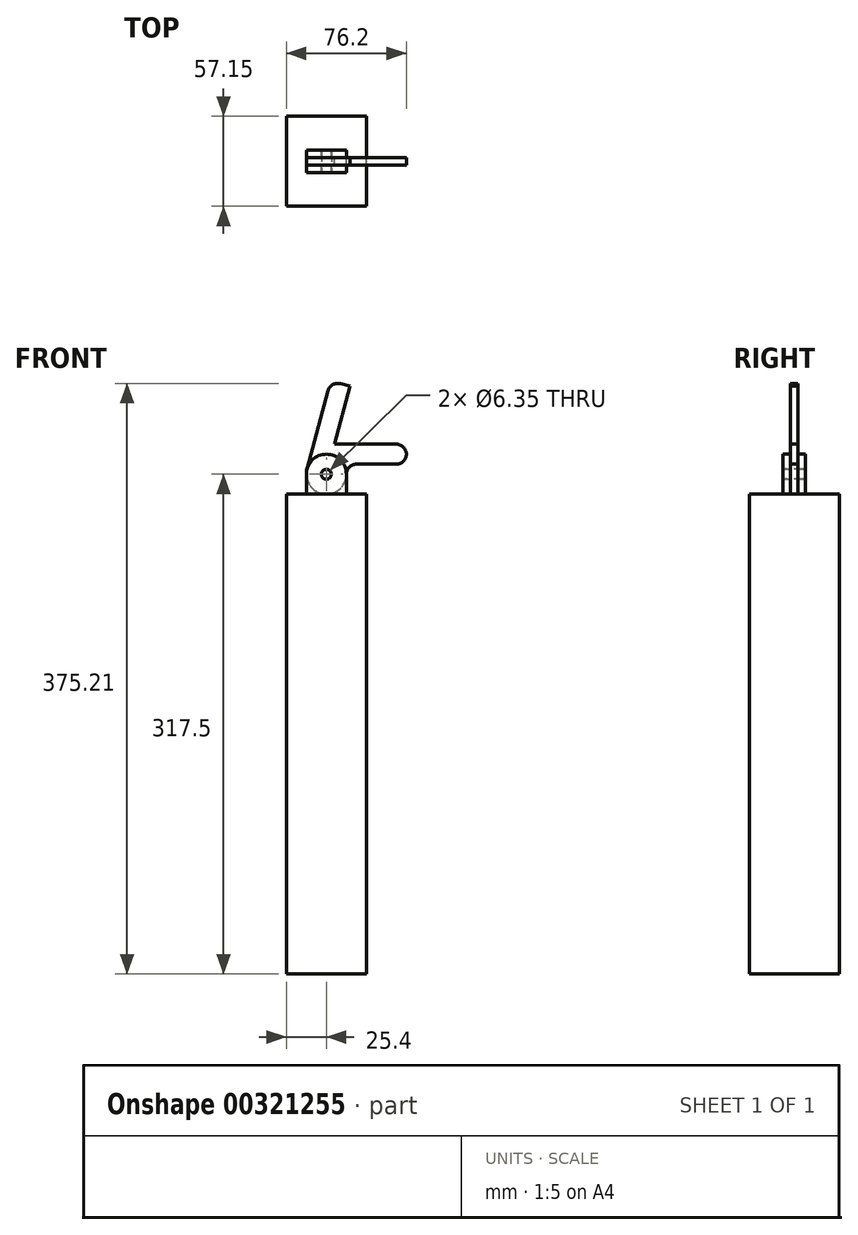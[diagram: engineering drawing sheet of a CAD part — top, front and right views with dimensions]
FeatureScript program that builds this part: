
annotation { "Feature Type Name" : "Feature", "Feature Type Description" : "" }
export const myFeature = defineFeature(function(context is Context, id is Id, definition is map)
    precondition{}
    {
        {
            var Q0;
            Q0=qCreatedBy(makeId("Front.planeOp"),FACE);
            var sketch = newSketch(context, id + "F0", { "sketchPlane" : qUnion([Q0])});
            skCircle(sketch, "E0", {"center": v(0, 0) * mm, "radius": 3.18 * mm});
            skArc(sketch, "E1", {"start": v(12.7, 0) * mm, "mid": v(0, 12.7) * mm, "end": v(-12.7, 0) * mm});
            skLineSegment(sketch, "E2", {"start": v(-12.7, 0) * mm, "end": v(-12.7, -12.7) * mm});
            skLineSegment(sketch, "E3", {"start": v(12.7, 0) * mm, "end": v(12.7, -12.7) * mm});
            skLineSegment(sketch, "E4", {"start": v(0, -12.7) * mm, "end": v(12.7, -12.7) * mm});
            skLineSegment(sketch, "E5", {"start": v(0, -12.7) * mm, "end": v(-12.7, -12.7) * mm});
            skSolve(sketch);
        }
        {
            var Q0;
            Q0=makeQuery(id+"F0.imprint","IMPRINT",FACE,{"disambiguationData":[TD([[makeQuery(id+"F0.imprint","IMPRINT",EDGE,{"derivedFrom":sQuery(id+"F0.wireOp",EDGE,"E0")}),-1.0]])]});
            extrude(context, id + "F1", {"entities" : qUnion([Q0]), "depth" : 4.76 * mm});
        }
        {
            var Q0;
            Q0=makeQuery(id+"F1.opExtrude","SWEPT_BODY",BODY,{"disambiguationData":[OSD([sQuery(id+"F0.wireOp",EDGE,"E0"),sQuery(id+"F0.wireOp",EDGE,"E1"),sQuery(id+"F0.wireOp",EDGE,"E2"),sQuery(id+"F0.wireOp",EDGE,"E3"),sQuery(id+"F0.wireOp",EDGE,"E4"),sQuery(id+"F0.wireOp",EDGE,"E5")])]});
            transform(context, id + "F2", {"entities" : qUnion([Q0]), "transformType" : TransformType.TRANSLATION_3D, "dx" : 0 * mm, "dy" : 9.52 * mm, "dz" : 0 * mm, "makeCopy" : true});
        }
        {
            var Q0;
            Q0=makeQuery(id+"F0.imprint","IMPRINT",FACE,{"disambiguationData":[TD([[makeQuery(id+"F0.imprint","IMPRINT",EDGE,{"derivedFrom":sQuery(id+"F0.wireOp",EDGE,"E0")}),1.0]])]});
            extrude(context, id + "F3", {"entities" : qUnion([Q0]), "oppositeDirection" : true, "depth" : 9.52 * mm, "hasSecondDirection" : true, "secondDirectionOppositeDirection" : false, "secondDirectionDepth" : 4.76 * mm});
        }
        {
            var Q0;
            Q0=makeQuery(id+"F2.opPattern","COPY",FACE,{"derivedFrom":makeQuery(id+"F1.opExtrude","CAP_FACE",FACE,{"disambiguationData":[OSD([sQuery(id+"F0.wireOp",EDGE,"E0"),sQuery(id+"F0.wireOp",EDGE,"E1"),sQuery(id+"F0.wireOp",EDGE,"E2"),sQuery(id+"F0.wireOp",EDGE,"E3"),sQuery(id+"F0.wireOp",EDGE,"E4"),sQuery(id+"F0.wireOp",EDGE,"E5")])],"isStart":false}),"instanceName":"1"});
            cPlane(context, id + "F4", {"entities" : qUnion([Q0]), "cplaneType" : CPlaneType.OFFSET, "offset" : 2.38 * mm, "width" : 152.4 * mm, "height" : 152.4 * mm});
        }
        {
            var Q0;
            Q0=qCreatedBy(id+"F4.planeOp",FACE);
            var sketch = newSketch(context, id + "F5", { "sketchPlane" : qUnion([Q0])});
            skLineSegment(sketch, "E6", {"start": v(50.8, 12.7) * mm, "end": v(50.8, 12.7) * mm});
            skLineSegment(sketch, "E7", {"start": v(44.45, 19.05) * mm, "end": v(5.1, 19.05) * mm});
            skPoint(sketch, "E8.visualSharp", {"position": v(50.8, 19.05) * mm});
            skArc(sketch, "E8.filletArc", {"start": v(50.8, 12.7) * mm, "mid": v(48.94, 17.2) * mm, "end": v(44.45, 19.05) * mm});
            skPoint(sketch, "E9.visualSharp", {"position": v(50.8, 6.35) * mm});
            skPoint(sketch, "E10.visualSharp", {"position": v(12.7, 0) * mm});
            skLineSegment(sketch, "E11", {"start": v(12.7, 0) * mm, "end": v(12.7, 0) * mm});
            skLineSegment(sketch, "E12", {"start": v(19.05, 6.35) * mm, "end": v(44.45, 6.35) * mm});
            skPoint(sketch, "E13.visualSharp", {"position": v(12.7, 6.35) * mm});
            skArc(sketch, "E13.filletArc", {"start": v(19.05, 6.35) * mm, "mid": v(14.56, 4.5) * mm, "end": v(12.7, 0) * mm});
            skArc(sketch, "E14.filletArc", {"start": v(44.45, 6.35) * mm, "mid": v(48.94, 8.2) * mm, "end": v(50.8, 12.7) * mm});
            skLineSegment(sketch, "E15", {"start": v(-12.27, 3.29) * mm, "end": v(1.05, 53) * mm});
            skLineSegment(sketch, "E16", {"start": v(8.83, 57.5) * mm, "end": v(14.97, 55.85) * mm});
            skLineSegment(sketch, "E17", {"start": v(14.97, 55.85) * mm, "end": v(5.1, 19.05) * mm});
            skArc(sketch, "E18", {"start": v(-12.27, 3.29) * mm, "mid": v(-1.66, -12.6) * mm, "end": v(12.7, 0) * mm});
            skPoint(sketch, "E19.visualSharp", {"position": v(2.7, 59.14) * mm});
            skArc(sketch, "E19.filletArc", {"start": v(8.83, 57.5) * mm, "mid": v(4.01, 56.86) * mm, "end": v(1.05, 53) * mm});
            skSolve(sketch);
        }
        {
            var Q0;
            Q0=makeQuery(id+"F5.imprint","IMPRINT",FACE,{"disambiguationData":[TD([[makeQuery(id+"F5.imprint","IMPRINT",EDGE,{"derivedFrom":sQuery(id+"F5.wireOp",EDGE,"ZBOrRvWA-Zsny-QJQH-aAW1-NDks2fAVxMMG")}),1.0]])]});
            var Q1;
            {var subQ1=sQuery(id+"F5.wireOp",EDGE,"qktoMMUk-6ylO-f5TV-pOuF-03LsLpky7e9K");Q1=makeQuery(id+"F5.imprint","IMPRINT",FACE,{"disambiguationData":[TD([[makeQuery(id+"F5.imprint","IMPRINT",EDGE,{"derivedFrom":subQ1}),1.0]])]});}
            var Q2;
            Q2=makeQuery(id+"F5.imprint","IMPRINT",FACE,{"disambiguationData":[TD([[makeQuery(id+"F5.imprint","IMPRINT",EDGE,{"derivedFrom":sQuery(id+"F5.wireOp",EDGE,"E7")}),1.0]])]});
            extrude(context, id + "F6", {"entities" : qUnion([Q0, Q1, Q2]), "endBound" : BoundingType.SYMMETRIC, "depth" : 4.76 * mm});
        }
        {
            var Q0;
            Q0=makeQuery(id+"F1.opExtrude","SWEPT_FACE",FACE,{"disambiguationData":[OSD([sQuery(id+"F0.wireOp",EDGE,"E4"),sQuery(id+"F0.wireOp",EDGE,"E5")])]});
            var sketch = newSketch(context, id + "F7", { "sketchPlane" : qUnion([Q0])});
            skLineSegment(sketch, "E20.bottom", {"start": v(-25.4, 26.2) * mm, "end": v(25.4, 26.2) * mm});
            skLineSegment(sketch, "E20.top", {"start": v(-25.4, -30.96) * mm, "end": v(25.4, -30.96) * mm});
            skLineSegment(sketch, "E20.left", {"start": v(-25.4, 26.2) * mm, "end": v(-25.4, -30.96) * mm});
            skLineSegment(sketch, "E20.right", {"start": v(25.4, 26.2) * mm, "end": v(25.4, -30.96) * mm});
            skSolve(sketch);
        }
        {
            var Q0;
            Q0=makeQuery(id+"F7.imprint","IMPRINT",FACE,{"disambiguationData":[TD([[makeQuery(id+"F7.imprint","IMPRINT",EDGE,{"derivedFrom":sQuery(id+"F7.wireOp",EDGE,"E20.bottom")}),-1.0]])]});
            var Q1;
            {var subQ0=sQuery(id+"F0.wireOp",EDGE,"E5");Q1=makeQuery(id+"F7.imprint","IMPRINT",FACE,{"disambiguationData":[TD([[makeQuery(id+"F7.imprint","IMPRINT",EDGE,{"derivedFrom":makeQuery(id+"F1.opExtrude","SWEPT_EDGE",EDGE,{"disambiguationData":[OSD([sQuery(id+"F0.wireOp",EDGE,"E2"),subQ0])]})}),1.0]])]});}
            extrude(context, id + "F8", {"entities" : qUnion([Q0, Q1]), "depth" : 304.8 * mm});
        }
    });
